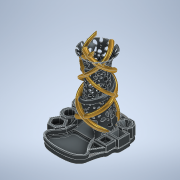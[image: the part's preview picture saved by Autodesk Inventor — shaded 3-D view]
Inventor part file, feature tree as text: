
AUTODESK INVENTOR PART (.ipt)
format: ipt  version: 2022 (Build 260153000, 153)  size: 9,739,776 bytes
history: native  units: mm
features: sketch x28, extrude x24, fillet x12, helix x5, plane x3, chamfer x3, revolve x2, pattern_circular x2
ambient origin geometry x8: Origin, YZ Plane, XZ Plane, XY Plane, X Axis, Y Axis, Z Axis, Center Point
bodies: Solid1 (feature_tree)
feature tree (79):
  revolve  "Revolution1"  [1 undecoded]
  plane  "Work Plane1"
  extrude  "Extrusion4"  Depth=20.0mm
  extrude  "Extrusion2"  Depth=19.0mm
  pattern_circular  "Circular Pattern2"  Count=11  [1 undecoded]
  plane  "Work Plane3"
  extrude  "Extrusion3"  Depth=10.0mm
  pattern_circular  "Circular Pattern3"  Count=7  [1 undecoded]
  helix  "Coil1"  [1 undecoded]
  helix  "Coil2"  [1 undecoded]
  helix  "Coil3"  [1 undecoded]
  helix  "Coil4"  [1 undecoded]
  helix  "Coil5"  [1 undecoded]
  extrude  "Extrusion5"  Depth=20.0mm
  revolve  "Revolution2"  [1 undecoded]
  extrude  "Extrusion6"  Depth=30.0mm
  extrude  "Extrusion7"  Depth=15.0mm
  extrude  "Extrusion15"  Depth=30.0mm
  extrude  "Extrusion16"  Depth=45.0mm
  extrude  "Extrusion17"  Depth=13.0mm
  extrude  "Extrusion18"  Depth=39.0mm
  extrude  "Extrusion19"  Depth=11.0mm
  extrude  "Extrusion20"  Depth=10.0mm
  extrude  "Extrusion21"  Depth=11.0mm
  extrude  "Extrusion22"  Depth=9.0mm
  extrude  "Extrusion23"  Depth=3.0mm TaperAngle=0.0deg
  extrude  "Extrusion25"  Depth=43.0mm
  fillet  "Fillet3"  [1 undecoded]
  extrude  "Extrusion26"  Depth=54.0mm TaperAngle=0.0deg
  extrude  "Extrusion27"  Depth=35.0mm
  extrude  "Extrusion28"  Depth=35.0mm
  extrude  "Extrusion29"  Depth=30.0mm
  extrude  "Extrusion30"  Depth=30.0mm
  extrude  "Extrusion31"  Depth=35.0mm
  extrude  "Extrusion32"  Depth=35.0mm
  chamfer  "Chamfer1"  Distance=5.0mm
  extrude  "Extrusion33"  Depth=10.0mm TaperAngle=0.0deg
  chamfer  "Chamfer2"  Distance=5.0mm
  chamfer  "Chamfer3"  Distance=10.0mm
  fillet  "Fillet4"  Radius=15.0mm
  fillet  "Fillet5"  Radius=0.2mm
  fillet  "Fillet6"  Radius=5.0mm
  fillet  "Fillet7"  Radius=10.0mm
  fillet  "Fillet8"  Radius=15.0mm
  fillet  "Fillet9"  Radius=10.0mm
  fillet  "Fillet10"  Radius=7.0mm
  fillet  "Fillet11"  Radius=3.6mm
  fillet  "Fillet12"  Radius=10.0mm
  fillet  "Fillet13"  Radius=20.0mm
  fillet  "Fillet14"  Radius=24.0mm
  sketch  "Sketch1"  dims[d11=60.0mm d12=40.0mm]
  sketch  "Sketch3"  dims[d13=20.0mm d14=20.0mm]
  plane  "Work Plane2"
  sketch  "Sketch4"  dims[d15=20.0mm d16=19.0mm d17=110.0mm]
  sketch  "Sketch5"  dims[d18=40.0mm d19=10.0mm]
  sketch  "Sketch7"  dims[d20=179.0mm]
  sketch  "Sketch8"  dims[d26=2.0mm]
  sketch  "Sketch9"  dims[d27=2.0mm]
  sketch  "Sketch10"  dims[d28=2.0mm]
  sketch  "Sketch11"  dims[d29=2.0mm]
  sketch  "Sketch13"  dims[d30=2.0mm]
  sketch  "Sketch16"  dims[d31=90.0deg d32=70.0mm d38=77.75mm d39=0.0mm d40=40.0mm d41=360.0deg d43=70.0mm d44=77.75mm d45=0.0mm d46=40.0mm d47=360.0deg]
  sketch  "Sketch17"  dims[d49=20.0mm d50=20.0mm]
  sketch  "Sketch20"  dims[d51=20.0mm d52=20.0mm]
  sketch  "Sketch21"  dims[d53=40.0mm d54=30.0mm]
  sketch  "Sketch22"  dims[d55=30.0mm d56=15.0mm]
  sketch  "Sketch23"  dims[d57=15.0mm d58=30.0mm]
  sketch  "Sketch26"  dims[d59=77.75mm d60=0.0mm d61=45.0mm]
  sketch  "Sketch27"  dims[d62=35.0mm]
  sketch  "Sketch28"  dims[d63=70.0mm d64=120.0mm d65=10.0mm d66=-0.567232mm d67=90.0deg d68=90.0deg d69=90.0deg d70=90.0deg d71=13.0mm]
  sketch  "Sketch30"  dims[d72=10.0mm d73=39.0mm]
  sketch  "Sketch31"  dims[d74=140.0mm d75=180.0mm d76=10.0mm d77=-0.645772mm d78=90.0deg d79=90.0deg d80=90.0deg d81=90.0deg d82=11.0mm]
  sketch  "Sketch33"  dims[d83=39.0mm d84=10.0mm]
  sketch  "Sketch35"  dims[d85=135.0mm d86=180.0mm d87=10.0mm d88=-0.645772mm d89=90.0deg d90=90.0deg d91=90.0deg d92=90.0deg d93=11.0mm]
  sketch  "Sketch37"  dims[d94=170.0mm d95=190.0mm d96=10.0mm d97=-0.645772mm d98=90.0deg d99=90.0deg d100=90.0deg d101=90.0deg d102=9.0mm]
  sketch  "Sketch38"  dims[d103=170.0mm d104=190.0mm d105=10.0mm d106=-0.645772mm d107=90.0deg d108=90.0deg d109=90.0deg d110=90.0deg d125=3.0mm d126=0.0mm]
  sketch  "Sketch39"  dims[d128=60.0mm d129=43.0mm d130=270.0deg]
  sketch  "Sketch40"  dims[d132=34.0mm d133=54.0mm d134=0.0mm]
  sketch  "Sketch41"  dims[d136=54.0mm d137=0.0mm d141=35.0mm d165=35.0mm d166=30.0mm d167=30.0mm d168=30.0mm d169=30.0mm d170=35.0mm d172=35.0mm d186=5.0mm d187=10.0mm d188=0.0mm d190=5.0mm d191=0.0mm d192=10.0mm d193=0.0mm d194=15.0mm d195=0.0mm d196=0.2mm d197=0.0mm d198=5.0mm d199=0.0mm d200=10.0mm d201=0.0mm d202=15.0mm d203=0.0mm d204=10.0mm d205=0.0mm d210=7.0mm d211=0.0mm d212=3.6mm d213=10.0mm d214=0.0mm d215=20.0mm d216=24.0mm d217=20.0mm d218=30.0mm d219=23.5mm d220=5.75mm d221=5.75mm d222=5.75mm d223=14.0mm d224=0.0mm d225=22.5mm d226=6.25mm d227=6.25mm d228=6.25mm d229=14.0mm d230=0.0mm d231=25.0mm d232=5.0mm d233=5.0mm d234=5.0mm d235=14.0mm d236=0.0mm d237=25.5mm d239=3.0mm d241=10.0mm d242=0.0mm d243=54.0mm d244=43.0mm d245=17.5mm d246=17.5mm d247=7.0mm d248=5.5mm d249=4.0mm d250=3.607976mm d251=10.0mm d252=0.0mm d253=21.0mm d254=21.0mm d255=5.0mm d256=4.0mm d257=5.0mm d258=24.0mm d259=0.0mm d260=10.0mm d261=2.0mm d262=45.0deg d263=25.0mm d266=5.0mm d267=5.0mm d268=12.0mm d269=0.0mm d270=11.0mm d271=2.0mm d272=45.0deg d273=12.0mm d274=2.0mm d275=45.0deg d276=35.0mm d277=3.0mm d278=5.0mm d279=5.0mm d280=5.0mm d281=2.0mm d282=2.0mm d283=1.56mm d284=1.0mm d285=1.0mm d286=1.0mm d287=1.0mm d288=1.0mm d289=1.0mm d290=1.0mm d291=1.0mm d135=0.0mm]
note: 10 required parameter values undecoded (feature->parameter linkage not recoverable at this tier; creation-order binding heuristic only, values carry confidence <= 0.55)